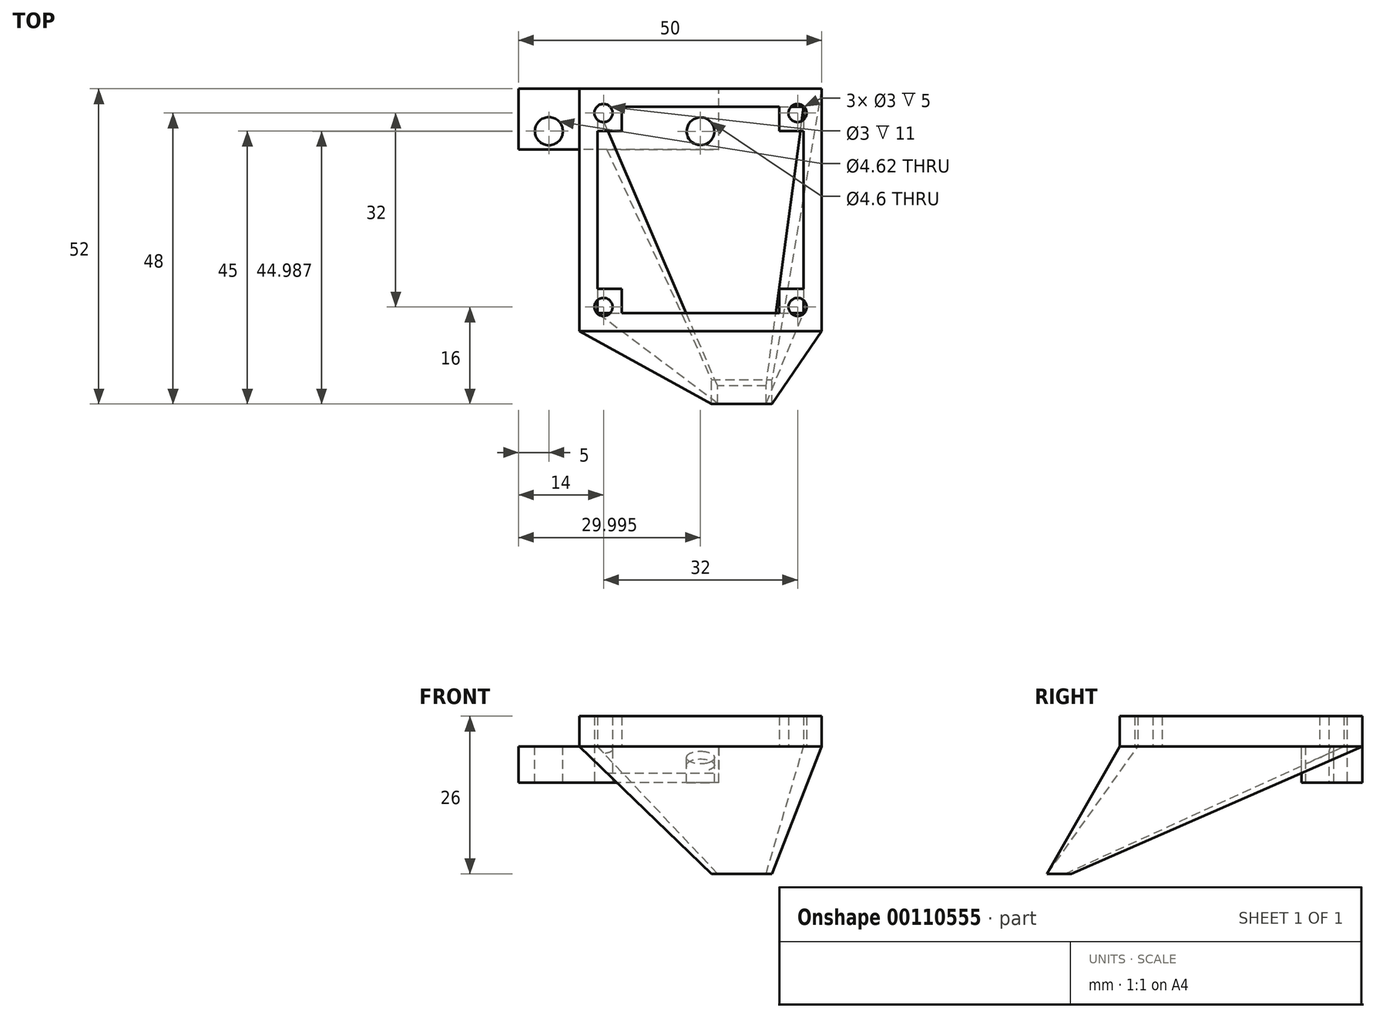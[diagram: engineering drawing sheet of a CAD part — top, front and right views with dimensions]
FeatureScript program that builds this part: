
annotation { "Feature Type Name" : "Feature", "Feature Type Description" : "" }
export const myFeature = defineFeature(function(context is Context, id is Id, definition is map)
    precondition{}
    {
        {
            var Q0;
            Q0=qCreatedBy(makeId("Top.planeOp"),FACE);
            var sketch = newSketch(context, id + "F0", { "sketchPlane" : qUnion([Q0])});
            skLineSegment(sketch, "E0.bottom", {"start": v(0, 0) * mm, "end": v(40, 0) * mm});
            skLineSegment(sketch, "E0.top", {"start": v(0, -40) * mm, "end": v(40, -40) * mm});
            skLineSegment(sketch, "E0.left", {"start": v(0, 0) * mm, "end": v(0, -40) * mm});
            skLineSegment(sketch, "E0.right", {"start": v(40, 0) * mm, "end": v(40, -40) * mm});
            skLineSegment(sketch, "E1.bottom", {"start": v(7, -3) * mm, "end": v(33, -3) * mm});
            skLineSegment(sketch, "E1.top", {"start": v(7, -37) * mm, "end": v(33, -37) * mm});
            skLineSegment(sketch, "E1.left", {"start": v(3, -7) * mm, "end": v(3, -33) * mm});
            skLineSegment(sketch, "E1.right", {"start": v(37, -7) * mm, "end": v(37, -33) * mm});
            skLineSegment(sketch, "E2.top", {"start": v(3, -7) * mm, "end": v(7, -7) * mm});
            skLineSegment(sketch, "E2.right", {"start": v(7, -3) * mm, "end": v(7, -7) * mm});
            skLineSegment(sketch, "E3.top", {"start": v(3, -33) * mm, "end": v(7, -33) * mm});
            skLineSegment(sketch, "E3.right", {"start": v(7, -37) * mm, "end": v(7, -33) * mm});
            skLineSegment(sketch, "E4.top", {"start": v(37, -33) * mm, "end": v(33, -33) * mm});
            skLineSegment(sketch, "E4.right", {"start": v(33, -37) * mm, "end": v(33, -33) * mm});
            skLineSegment(sketch, "E5.top", {"start": v(37, -7) * mm, "end": v(33, -7) * mm});
            skLineSegment(sketch, "E5.right", {"start": v(33, -3) * mm, "end": v(33, -7) * mm});
            skCircle(sketch, "E6", {"center": v(4, -4) * mm, "radius": 1.5 * mm});
            skCircle(sketch, "E7", {"center": v(4, -36) * mm, "radius": 1.5 * mm});
            skCircle(sketch, "E8", {"center": v(36, -4) * mm, "radius": 1.5 * mm});
            skCircle(sketch, "E9", {"center": v(36, -36) * mm, "radius": 1.5 * mm});
            skSolve(sketch);
        }
        {
            var Q0;
            Q0 = qSketchRegion(id + "F0", true);
            extrude(context, id + "F1", {"entities" : qUnion([Q0]), "depth" : 5 * mm});
        }
        {
            var Q0;
            Q0=qCreatedBy(makeId("Top.planeOp"),FACE);
            cPlane(context, id + "F2", {"entities" : qUnion([Q0]), "cplaneType" : CPlaneType.OFFSET, "offset" : 21 * mm, "oppositeDirection" : true, "width" : 150 * mm, "height" : 150 * mm});
        }
        {
            var Q0;
            Q0=qCreatedBy(id+"F2.planeOp",FACE);
            var sketch = newSketch(context, id + "F3", { "sketchPlane" : qUnion([Q0])});
            skLineSegment(sketch, "E10.bottom", {"start": v(21.8, -52) * mm, "end": v(31.8, -52) * mm});
            skLineSegment(sketch, "E10.top", {"start": v(21.8, -48) * mm, "end": v(31.8, -48) * mm});
            skLineSegment(sketch, "E10.left", {"start": v(21.8, -52) * mm, "end": v(21.8, -48) * mm});
            skLineSegment(sketch, "E10.right", {"start": v(31.8, -52) * mm, "end": v(31.8, -48) * mm});
            skLineSegment(sketch, "E11", {"start": v(26.8, -26.66) * mm, "end": v(26.8, -45.98) * mm, "construction": true});
            skPoint(sketch, "E11.startSnap0", {"position": v(26.8, -48) * mm});
            skPoint(sketch, "E11.endSnap0", {"position": v(26.8, -52) * mm});
            skSolve(sketch);
        }
        {
            var Q0;
            Q0=makeQuery(id+"F1.opExtrude","CAP_FACE",FACE,{"disambiguationData":[OSD([sQuery(id+"F0.wireOp",EDGE,"E0.bottom"),sQuery(id+"F0.wireOp",EDGE,"E0.top"),sQuery(id+"F0.wireOp",EDGE,"E0.left"),sQuery(id+"F0.wireOp",EDGE,"E0.right"),sQuery(id+"F0.wireOp",EDGE,"E1.bottom"),sQuery(id+"F0.wireOp",EDGE,"E1.top"),sQuery(id+"F0.wireOp",EDGE,"E1.left"),sQuery(id+"F0.wireOp",EDGE,"E1.right"),sQuery(id+"F0.wireOp",EDGE,"E2.top"),sQuery(id+"F0.wireOp",EDGE,"E2.right"),sQuery(id+"F0.wireOp",EDGE,"E3.top"),sQuery(id+"F0.wireOp",EDGE,"E3.right"),sQuery(id+"F0.wireOp",EDGE,"E4.top"),sQuery(id+"F0.wireOp",EDGE,"E4.right"),sQuery(id+"F0.wireOp",EDGE,"E5.top"),sQuery(id+"F0.wireOp",EDGE,"E5.right"),sQuery(id+"F0.wireOp",EDGE,"E6"),sQuery(id+"F0.wireOp",EDGE,"E7"),sQuery(id+"F0.wireOp",EDGE,"E8"),sQuery(id+"F0.wireOp",EDGE,"E9")])],"isStart":true});
            var sketch = newSketch(context, id + "F4", { "sketchPlane" : qUnion([Q0])});
            skLineSegment(sketch, "E12.bottom", {"start": v(0, 40) * mm, "end": v(40, 40) * mm});
            skLineSegment(sketch, "E12.top", {"start": v(0, 0) * mm, "end": v(40, 0) * mm});
            skLineSegment(sketch, "E12.left", {"start": v(0, 40) * mm, "end": v(0, 0) * mm});
            skLineSegment(sketch, "E12.right", {"start": v(40, 40) * mm, "end": v(40, 0) * mm});
            skSolve(sketch);
        }
        {
            var Q1;
            Q1 = qSketchRegion(id + "F4", true);
            var Q2;
            Q2 = qSketchRegion(id + "F3", true);
            loft(context, id + "F5", {"sheetProfilesArray" : [{ "sheetProfileEntities" : qUnion([Q1]) }, { "sheetProfileEntities" : qUnion([Q2]) }]});
        }
        {
            var Q0;
            Q0=makeQuery(id+"F1.opExtrude","CAP_FACE",FACE,{"disambiguationData":[OSD([sQuery(id+"F0.wireOp",EDGE,"E0.bottom"),sQuery(id+"F0.wireOp",EDGE,"E0.top"),sQuery(id+"F0.wireOp",EDGE,"E0.left"),sQuery(id+"F0.wireOp",EDGE,"E0.right"),sQuery(id+"F0.wireOp",EDGE,"E1.bottom"),sQuery(id+"F0.wireOp",EDGE,"E1.top"),sQuery(id+"F0.wireOp",EDGE,"E1.left"),sQuery(id+"F0.wireOp",EDGE,"E1.right"),sQuery(id+"F0.wireOp",EDGE,"E2.top"),sQuery(id+"F0.wireOp",EDGE,"E2.right"),sQuery(id+"F0.wireOp",EDGE,"E3.top"),sQuery(id+"F0.wireOp",EDGE,"E3.right"),sQuery(id+"F0.wireOp",EDGE,"E4.top"),sQuery(id+"F0.wireOp",EDGE,"E4.right"),sQuery(id+"F0.wireOp",EDGE,"E5.top"),sQuery(id+"F0.wireOp",EDGE,"E5.right"),sQuery(id+"F0.wireOp",EDGE,"E6"),sQuery(id+"F0.wireOp",EDGE,"E7"),sQuery(id+"F0.wireOp",EDGE,"E8"),sQuery(id+"F0.wireOp",EDGE,"E9")])],"isStart":true});
            var sketch = newSketch(context, id + "F6", { "sketchPlane" : qUnion([Q0])});
            skLineSegment(sketch, "E13.bottom", {"start": v(23, 10) * mm, "end": v(-10, 10) * mm});
            skLineSegment(sketch, "E13.top", {"start": v(23, 0) * mm, "end": v(-10, 0) * mm});
            skLineSegment(sketch, "E13.left", {"start": v(23, 10) * mm, "end": v(23, 0) * mm});
            skLineSegment(sketch, "E13.right", {"start": v(-10, 10) * mm, "end": v(-10, 0) * mm});
            skCircle(sketch, "E14", {"center": v(-5, 7) * mm, "radius": 2.3 * mm});
            skCircle(sketch, "E15", {"center": v(20, 7) * mm, "radius": 2.3 * mm});
            skSolve(sketch);
        }
        {
            var Q0;
            Q0 = qSketchRegion(id + "F6", true);
            extrude(context, id + "F7", {"entities" : qUnion([Q0]), "operationType" : NewBodyOperationType.ADD, "depth" : 6 * mm});
        }
        {
            var Q0;
            Q0=makeQuery(id+"F5.opLoft","CAP_FACE",FACE,{"disambiguationData":[OSD([makeQuery(id+"F3.imprint","IMPRINT",FACE,{"disambiguationData":[TD([[makeQuery(id+"F3.imprint","IMPRINT",EDGE,{"derivedFrom":sQuery(id+"F3.wireOp",EDGE,"E10.bottom")}),1.0]])]})])],"isStart":true});
            var sketch = newSketch(context, id + "F8", { "sketchPlane" : qUnion([Q0])});
            skLineSegment(sketch, "E16.bottom", {"start": v(30.8, 51.9) * mm, "end": v(22.8, 51.9) * mm});
            skLineSegment(sketch, "E16.top", {"start": v(30.8, 49) * mm, "end": v(22.8, 49) * mm});
            skLineSegment(sketch, "E16.left", {"start": v(30.8, 51.9) * mm, "end": v(30.8, 49) * mm});
            skLineSegment(sketch, "E16.right", {"start": v(22.8, 51.9) * mm, "end": v(22.8, 49) * mm});
            skSolve(sketch);
        }
        {
            var Q0;
            Q0=makeQuery(id+"F5.opLoft","CAP_FACE",FACE,{"disambiguationData":[OSD([makeQuery(id+"F4.imprint","IMPRINT",FACE,{"disambiguationData":[TD([[makeQuery(id+"F4.imprint","IMPRINT",EDGE,{"derivedFrom":sQuery(id+"F4.wireOp",EDGE,"E12.bottom")}),-1.0]])]})])],"isStart":true});
            var sketch = newSketch(context, id + "F9", { "sketchPlane" : qUnion([Q0])});
            skLineSegment(sketch, "E17.bottom", {"start": v(3, -3) * mm, "end": v(37, -3) * mm});
            skLineSegment(sketch, "E17.top", {"start": v(3, -37) * mm, "end": v(37, -37) * mm});
            skLineSegment(sketch, "E17.left", {"start": v(3, -3) * mm, "end": v(3, -37) * mm});
            skLineSegment(sketch, "E17.right", {"start": v(37, -3) * mm, "end": v(37, -37) * mm});
            skSolve(sketch);
        }
        {
            var Q1;
            Q1 = qSketchRegion(id + "F8", true);
            var Q2;
            Q2 = qSketchRegion(id + "F9", true);
            loft(context, id + "F10", {"operationType" : NewBodyOperationType.REMOVE, "sheetProfilesArray" : [{ "sheetProfileEntities" : qUnion([Q1]) }, { "sheetProfileEntities" : qUnion([Q2]) }]});
        }
        {
            var Q0;
            Q0=qCreatedBy(makeId("Front.planeOp"),FACE);
            cPlane(context, id + "F11", {"entities" : qUnion([Q0]), "cplaneType" : CPlaneType.OFFSET, "offset" : 39 * mm, "width" : 150 * mm, "height" : 150 * mm});
        }
        {
            var Q0;
            Q0=makeQuery(id+"F1.opExtrude","CAP_FACE",FACE,{"disambiguationData":[OSD([sQuery(id+"F0.wireOp",EDGE,"E0.bottom"),sQuery(id+"F0.wireOp",EDGE,"E0.top"),sQuery(id+"F0.wireOp",EDGE,"E0.left"),sQuery(id+"F0.wireOp",EDGE,"E0.right"),sQuery(id+"F0.wireOp",EDGE,"E1.bottom"),sQuery(id+"F0.wireOp",EDGE,"E1.top"),sQuery(id+"F0.wireOp",EDGE,"E1.left"),sQuery(id+"F0.wireOp",EDGE,"E1.right"),sQuery(id+"F0.wireOp",EDGE,"E2.top"),sQuery(id+"F0.wireOp",EDGE,"E2.right"),sQuery(id+"F0.wireOp",EDGE,"E3.top"),sQuery(id+"F0.wireOp",EDGE,"E3.right"),sQuery(id+"F0.wireOp",EDGE,"E4.top"),sQuery(id+"F0.wireOp",EDGE,"E4.right"),sQuery(id+"F0.wireOp",EDGE,"E5.top"),sQuery(id+"F0.wireOp",EDGE,"E5.right"),sQuery(id+"F0.wireOp",EDGE,"E6"),sQuery(id+"F0.wireOp",EDGE,"E7"),sQuery(id+"F0.wireOp",EDGE,"E8"),sQuery(id+"F0.wireOp",EDGE,"E9")])],"isStart":false});
            var sketch = newSketch(context, id + "F12", { "sketchPlane" : qUnion([Q0])});
            skCircle(sketch, "E18", {"center": v(4, -4) * mm, "radius": 1.5 * mm});
            skCircle(sketch, "E19", {"center": v(20, -7.01) * mm, "radius": 2.3 * mm});
            skSolve(sketch);
        }
        {
            var Q0;
            Q0 = qSketchRegion(id + "F12", true);
            extrude(context, id + "F13", {"entities" : qUnion([Q0]), "operationType" : NewBodyOperationType.REMOVE, "oppositeDirection" : true, "depth" : 25 * mm});
        }
    });
